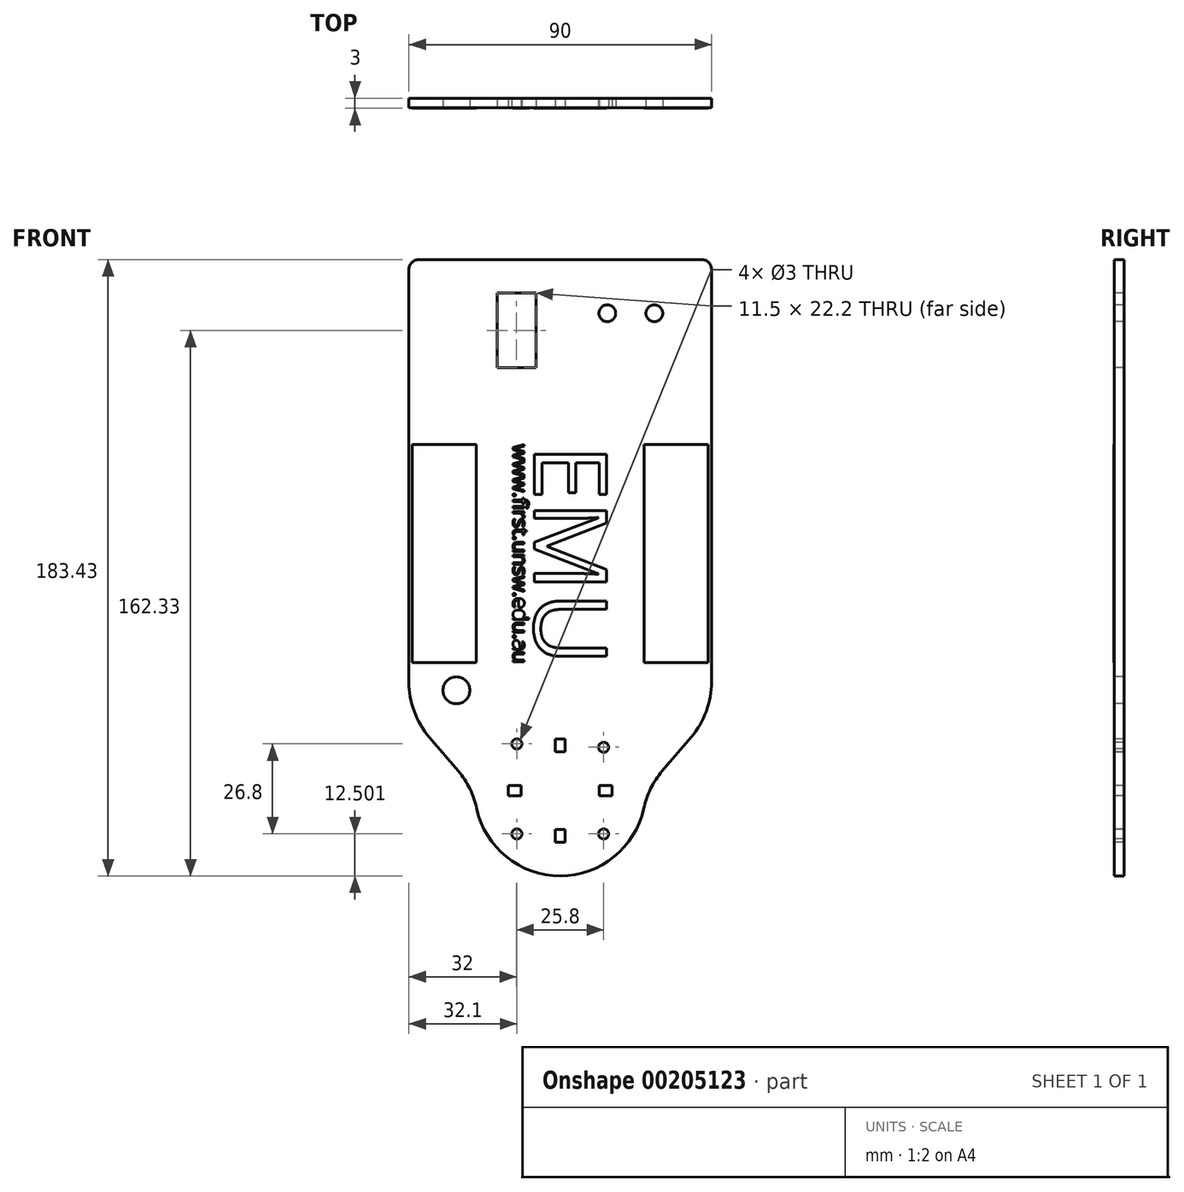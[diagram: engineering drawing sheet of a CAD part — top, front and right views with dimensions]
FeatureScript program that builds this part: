
annotation { "Feature Type Name" : "Feature", "Feature Type Description" : "" }
export const myFeature = defineFeature(function(context is Context, id is Id, definition is map)
    precondition{}
    {
        {
            var Q0;
            Q0=qCreatedBy(makeId("Front.planeOp"),FACE);
            var sketch = newSketch(context, id + "F0", { "sketchPlane" : qUnion([Q0])});
            skLineSegment(sketch, "E0.bottom", {"start": v(0, 0) * mm, "end": v(-90, 0) * mm});
            skLineSegment(sketch, "E0.top", {"start": v(0, 135) * mm, "end": v(-90, 135) * mm});
            skLineSegment(sketch, "E0.left", {"start": v(0, 0) * mm, "end": v(0, 135) * mm});
            skLineSegment(sketch, "E0.right", {"start": v(-90, 0) * mm, "end": v(-90, 135) * mm});
            skLineSegment(sketch, "E1", {"start": v(-90, 0) * mm, "end": v(-45, -70) * mm});
            skLineSegment(sketch, "E2", {"start": v(-45, -70) * mm, "end": v(0, 0) * mm});
            skSolve(sketch);
        }
        {
            var Q0;
            Q0=makeQuery(id+"F0.imprint","IMPRINT",FACE,{"disambiguationData":[TD([[makeQuery(id+"F0.imprint","IMPRINT",EDGE,{"derivedFrom":sQuery(id+"F0.wireOp",EDGE,"E0.bottom")}),-1.0]])]});
            var Q1;
            Q1=makeQuery(id+"F0.imprint","IMPRINT",FACE,{"disambiguationData":[TD([[makeQuery(id+"F0.imprint","IMPRINT",EDGE,{"derivedFrom":sQuery(id+"F0.wireOp",EDGE,"E0.bottom")}),1.0]])]});
            extrude(context, id + "F1", {"entities" : qUnion([Q0, Q1]), "depth" : 3 * mm});
        }
        {
            var Q0;
            Q0=makeQuery(id+"F1.opExtrude","CAP_FACE",FACE,{"disambiguationData":[OSD([sQuery(id+"F0.wireOp",EDGE,"E0.top"),sQuery(id+"F0.wireOp",EDGE,"E0.left"),sQuery(id+"F0.wireOp",EDGE,"E0.right"),sQuery(id+"F0.wireOp",EDGE,"E1"),sQuery(id+"F0.wireOp",EDGE,"E2")])],"isStart":false});
            var sketch = newSketch(context, id + "F2", { "sketchPlane" : qUnion([Q0])});
            skLineSegment(sketch, "E3.bottom", {"start": v(-63.75, 125) * mm, "end": v(-52.25, 125) * mm});
            skLineSegment(sketch, "E3.top", {"start": v(-63.75, 102.8) * mm, "end": v(-52.25, 102.8) * mm});
            skLineSegment(sketch, "E3.left", {"start": v(-63.75, 125) * mm, "end": v(-63.75, 102.8) * mm});
            skLineSegment(sketch, "E3.right", {"start": v(-52.25, 125) * mm, "end": v(-52.25, 102.8) * mm});
            skCircle(sketch, "E4", {"center": v(-58, 127) * mm, "radius": 1 * mm});
            skCircle(sketch, "E5", {"center": v(-58, 100.8) * mm, "radius": 1 * mm});
            skLineSegment(sketch, "E6", {"start": v(-59, 127) * mm, "end": v(-59, 125) * mm});
            skLineSegment(sketch, "E7", {"start": v(-57, 127) * mm, "end": v(-57, 125) * mm});
            skLineSegment(sketch, "E8", {"start": v(-59, 100.8) * mm, "end": v(-59, 102.8) * mm});
            skLineSegment(sketch, "E9", {"start": v(-57, 102.8) * mm, "end": v(-57, 100.8) * mm});
            skLineSegment(sketch, "E10", {"start": v(-45, 135) * mm, "end": v(-45, -52.75) * mm});
            skLineSegment(sketch, "E11", {"start": v(-58, 125) * mm, "end": v(-58, 102.8) * mm});
            skLineSegment(sketch, "E12", {"start": v(-63.75, 119) * mm, "end": v(-52.25, 119) * mm});
            skCircle(sketch, "E13", {"center": v(-31, 119) * mm, "radius": 2.5 * mm});
            skCircle(sketch, "E14", {"center": v(-17, 119) * mm, "radius": 2.5 * mm});
            skSolve(sketch);
        }
        {
            var Q0;
            {var subQ0=sQuery(id+"F2.wireOp",EDGE,"E3.left");Q0=makeQuery(id+"F2.imprint","IMPRINT",FACE,{"disambiguationData":[TD([[makeQuery(id+"F2.imprint","IMPRINT",EDGE,{"derivedFrom":subQ0}),1.0]])]});}
            var Q1;
            {var subQ1=sQuery(id+"F2.wireOp",EDGE,"E3.bottom");var subQ8=makeQuery(id+"F2.imprint","INTERSECT",VERTEX,{"derivedFrom":[subQ1,sQuery(id+"F2.wireOp",EDGE,"E7")]});Q1=makeQuery(id+"F2.imprint","IMPRINT",FACE,{"disambiguationData":[TD([[makeQuery(id+"F2.imprint","IMPRINT",EDGE,{"disambiguationData":[TD([[subQ8,1.0]])],"derivedFrom":subQ1}),-1.0]])]});}
            var Q2;
            {var subQ1=sQuery(id+"F2.wireOp",EDGE,"E3.top");var subQ7=makeQuery(id+"F2.imprint","INTERSECT",VERTEX,{"derivedFrom":[subQ1,sQuery(id+"F2.wireOp",EDGE,"E9")]});Q2=makeQuery(id+"F2.imprint","IMPRINT",FACE,{"disambiguationData":[TD([[makeQuery(id+"F2.imprint","IMPRINT",EDGE,{"disambiguationData":[TD([[subQ7,1.0]])],"derivedFrom":subQ1}),1.0]])]});}
            var Q3;
            Q3=makeQuery(id+"F2.imprint","IMPRINT",FACE,{"disambiguationData":[TD([[makeQuery(id+"F2.imprint","IMPRINT",EDGE,{"derivedFrom":sQuery(id+"F2.wireOp",EDGE,"E13")}),1.0]])]});
            var Q4;
            Q4=makeQuery(id+"F2.imprint","IMPRINT",FACE,{"disambiguationData":[TD([[makeQuery(id+"F2.imprint","IMPRINT",EDGE,{"derivedFrom":sQuery(id+"F2.wireOp",EDGE,"E14")}),1.0]])]});
            extrude(context, id + "F3", {"entities" : qUnion([Q0, Q1, Q2, Q3, Q4]), "operationType" : NewBodyOperationType.REMOVE, "oppositeDirection" : true, "depth" : 25.4 * mm});
        }
        {
            var Q0;
            Q0=makeQuery(id+"F1.opExtrude","SWEPT_EDGE",EDGE,{"disambiguationData":[OSD([sQuery(id+"F0.wireOp",EDGE,"E1"),sQuery(id+"F0.wireOp",EDGE,"E2")])]});
            fillet(context, id + "F4", {"entities" : qUnion([Q0]), "radius" : 25.4 * mm, "tangentPropagation" : true, "allowEdgeOverflow" : false});
        }
        {
            var Q0;
            Q0=makeQuery(id+"F1.opExtrude","CAP_FACE",FACE,{"disambiguationData":[OSD([sQuery(id+"F0.wireOp",EDGE,"E0.top"),sQuery(id+"F0.wireOp",EDGE,"E0.left"),sQuery(id+"F0.wireOp",EDGE,"E0.right"),sQuery(id+"F0.wireOp",EDGE,"E1"),sQuery(id+"F0.wireOp",EDGE,"E2")])],"isStart":false});
            var sketch = newSketch(context, id + "F5", { "sketchPlane" : qUnion([Q0])});
            skCircle(sketch, "E15", {"center": v(-45, -23.03) * mm, "radius": 25.4 * mm});
            skLineSegment(sketch, "E16", {"start": v(-45, -48.43) * mm, "end": v(-45, 2.37) * mm});
            skLineSegment(sketch, "E17", {"start": v(-45, -23.03) * mm, "end": v(-19.6, -23.03) * mm});
            skLineSegment(sketch, "E18", {"start": v(-45, -23.03) * mm, "end": v(-70.4, -23.03) * mm});
            skLineSegment(sketch, "E19.bottom", {"start": v(-60.4, -24.53) * mm, "end": v(-56.59, -24.53) * mm});
            skLineSegment(sketch, "E19.top", {"start": v(-60.4, -21.53) * mm, "end": v(-56.59, -21.53) * mm});
            skLineSegment(sketch, "E19.left", {"start": v(-60.4, -24.53) * mm, "end": v(-60.4, -21.53) * mm});
            skLineSegment(sketch, "E19.right", {"start": v(-56.59, -24.53) * mm, "end": v(-56.59, -21.53) * mm});
            skLineSegment(sketch, "E20.bottom", {"start": v(-46.5, -11.44) * mm, "end": v(-43.5, -11.44) * mm});
            skLineSegment(sketch, "E20.top", {"start": v(-46.5, -7.63) * mm, "end": v(-43.5, -7.63) * mm});
            skLineSegment(sketch, "E20.left", {"start": v(-46.5, -11.44) * mm, "end": v(-46.5, -7.63) * mm});
            skLineSegment(sketch, "E20.right", {"start": v(-43.5, -11.44) * mm, "end": v(-43.5, -7.63) * mm});
            skLineSegment(sketch, "E21.bottom", {"start": v(-33.4, -21.53) * mm, "end": v(-29.6, -21.53) * mm});
            skLineSegment(sketch, "E21.top", {"start": v(-33.4, -24.53) * mm, "end": v(-29.6, -24.53) * mm});
            skLineSegment(sketch, "E21.left", {"start": v(-33.4, -21.53) * mm, "end": v(-33.4, -24.53) * mm});
            skLineSegment(sketch, "E21.right", {"start": v(-29.6, -21.53) * mm, "end": v(-29.6, -24.53) * mm});
            skLineSegment(sketch, "E22.bottom", {"start": v(-46.5, -34.62) * mm, "end": v(-43.5, -34.62) * mm});
            skLineSegment(sketch, "E22.top", {"start": v(-46.5, -38.43) * mm, "end": v(-43.5, -38.43) * mm});
            skLineSegment(sketch, "E22.left", {"start": v(-46.5, -34.62) * mm, "end": v(-46.5, -38.43) * mm});
            skLineSegment(sketch, "E22.right", {"start": v(-43.5, -34.62) * mm, "end": v(-43.5, -38.43) * mm});
            skLineSegment(sketch, "E23", {"start": v(-45, -3.98) * mm, "end": v(-45, -11.44) * mm});
            skCircle(sketch, "E24", {"center": v(-57.9, -9.13) * mm, "radius": 1.5 * mm});
            skCircle(sketch, "E25", {"center": v(-32.1, -10.13) * mm, "radius": 1.5 * mm});
            skCircle(sketch, "E26", {"center": v(-32.1, -35.93) * mm, "radius": 1.5 * mm});
            skCircle(sketch, "E27", {"center": v(-57.9, -35.93) * mm, "radius": 1.5 * mm});
            skSolve(sketch);
        }
        {
            var Q0;
            {var subQ5=sQuery(id+"F5.wireOp",EDGE,"E19.top");Q0=makeQuery(id+"F5.imprint","IMPRINT",FACE,{"disambiguationData":[TD([[makeQuery(id+"F5.imprint","IMPRINT",EDGE,{"derivedFrom":subQ5}),-1.0]])]});}
            var Q1;
            {var subQ5=sQuery(id+"F5.wireOp",EDGE,"E19.bottom");Q1=makeQuery(id+"F5.imprint","IMPRINT",FACE,{"disambiguationData":[TD([[makeQuery(id+"F5.imprint","IMPRINT",EDGE,{"derivedFrom":subQ5}),1.0]])]});}
            var Q2;
            {var subQ5=sQuery(id+"F5.wireOp",EDGE,"E21.bottom");Q2=makeQuery(id+"F5.imprint","IMPRINT",FACE,{"disambiguationData":[TD([[makeQuery(id+"F5.imprint","IMPRINT",EDGE,{"derivedFrom":subQ5}),-1.0]])]});}
            var Q3;
            {var subQ5=sQuery(id+"F5.wireOp",EDGE,"E21.top");Q3=makeQuery(id+"F5.imprint","IMPRINT",FACE,{"disambiguationData":[TD([[makeQuery(id+"F5.imprint","IMPRINT",EDGE,{"derivedFrom":subQ5}),1.0]])]});}
            var Q4;
            {var subQ5=sQuery(id+"F5.wireOp",EDGE,"E22.right");Q4=makeQuery(id+"F5.imprint","IMPRINT",FACE,{"disambiguationData":[TD([[makeQuery(id+"F5.imprint","IMPRINT",EDGE,{"derivedFrom":subQ5}),-1.0]])]});}
            var Q5;
            {var subQ5=sQuery(id+"F5.wireOp",EDGE,"E22.left");Q5=makeQuery(id+"F5.imprint","IMPRINT",FACE,{"disambiguationData":[TD([[makeQuery(id+"F5.imprint","IMPRINT",EDGE,{"derivedFrom":subQ5}),1.0]])]});}
            var Q6;
            {var subQ5=sQuery(id+"F5.wireOp",EDGE,"E20.right");Q6=makeQuery(id+"F5.imprint","IMPRINT",FACE,{"disambiguationData":[TD([[makeQuery(id+"F5.imprint","IMPRINT",EDGE,{"derivedFrom":subQ5}),1.0]])]});}
            var Q7;
            {var subQ5=sQuery(id+"F5.wireOp",EDGE,"E20.left");Q7=makeQuery(id+"F5.imprint","IMPRINT",FACE,{"disambiguationData":[TD([[makeQuery(id+"F5.imprint","IMPRINT",EDGE,{"derivedFrom":subQ5}),-1.0]])]});}
            var Q8;
            {var subQ5=sQuery(id+"F5.wireOp",EDGE,"Zrzo9GHM-fuN2-8fML-iVZU-LCXHQRcVOfyt.left");Q8=makeQuery(id+"F5.imprint","IMPRINT",FACE,{"disambiguationData":[TD([[makeQuery(id+"F5.imprint","IMPRINT",EDGE,{"derivedFrom":subQ5}),1.0]])]});}
            var Q9;
            {var subQ5=sQuery(id+"F5.wireOp",EDGE,"Zrzo9GHM-fuN2-8fML-iVZU-LCXHQRcVOfyt.right");Q9=makeQuery(id+"F5.imprint","IMPRINT",FACE,{"disambiguationData":[TD([[makeQuery(id+"F5.imprint","IMPRINT",EDGE,{"derivedFrom":subQ5}),-1.0]])]});}
            var Q10;
            {var subQ0=sQuery(id+"F5.wireOp",EDGE,"2EuhVOSW-e1DR-vE8P-bMp6-yslpzd3IsdpB");var subQ4=makeQuery(id+"F5.imprint","IMPRINT",VERTEX,{"derivedFrom":subQ0});Q10=makeQuery(id+"F5.imprint","IMPRINT",FACE,{"disambiguationData":[TD([[makeQuery(id+"F5.imprint","IMPRINT",EDGE,{"disambiguationData":[TD([[subQ4,1.0]])],"derivedFrom":subQ0}),-1.0]])]});}
            var Q11;
            {var subQ0=sQuery(id+"F5.wireOp",EDGE,"2EuhVOSW-e1DR-vE8P-bMp6-yslpzd3IsdpB");var subQ4=makeQuery(id+"F5.imprint","IMPRINT",VERTEX,{"derivedFrom":subQ0});Q11=makeQuery(id+"F5.imprint","IMPRINT",FACE,{"disambiguationData":[TD([[makeQuery(id+"F5.imprint","IMPRINT",EDGE,{"disambiguationData":[TD([[subQ4,1.0]])],"derivedFrom":subQ0}),1.0]])]});}
            var Q12;
            Q12=makeQuery(id+"F5.imprint","IMPRINT",FACE,{"disambiguationData":[TD([[makeQuery(id+"F5.imprint","IMPRINT",EDGE,{"derivedFrom":sQuery(id+"F5.wireOp",EDGE,"E24")}),1.0]])]});
            var Q13;
            Q13=makeQuery(id+"F5.imprint","IMPRINT",FACE,{"disambiguationData":[TD([[makeQuery(id+"F5.imprint","IMPRINT",EDGE,{"derivedFrom":sQuery(id+"F5.wireOp",EDGE,"E25")}),1.0]])]});
            var Q14;
            Q14=makeQuery(id+"F5.imprint","IMPRINT",FACE,{"disambiguationData":[TD([[makeQuery(id+"F5.imprint","IMPRINT",EDGE,{"derivedFrom":sQuery(id+"F5.wireOp",EDGE,"E26")}),1.0]])]});
            var Q15;
            Q15=makeQuery(id+"F5.imprint","IMPRINT",FACE,{"disambiguationData":[TD([[makeQuery(id+"F5.imprint","IMPRINT",EDGE,{"derivedFrom":sQuery(id+"F5.wireOp",EDGE,"E27")}),1.0]])]});
            extrude(context, id + "F6", {"entities" : qUnion([Q0, Q1, Q2, Q3, Q4, Q5, Q6, Q7, Q8, Q9, Q10, Q11, Q12, Q13, Q14, Q15]), "operationType" : NewBodyOperationType.REMOVE, "oppositeDirection" : true, "depth" : 25.4 * mm});
        }
        {
            var Q0;
            Q0=makeQuery(id+"F1.opExtrude","SWEPT_EDGE",EDGE,{"disambiguationData":[OSD([sQuery(id+"F0.wireOp",EDGE,"E0.top"),sQuery(id+"F0.wireOp",EDGE,"E0.left")])]});
            var Q1;
            Q1=makeQuery(id+"F1.opExtrude","SWEPT_EDGE",EDGE,{"disambiguationData":[OSD([sQuery(id+"F0.wireOp",EDGE,"E0.top"),sQuery(id+"F0.wireOp",EDGE,"E0.right")])]});
            fillet(context, id + "F7", {"entities" : qUnion([Q0, Q1]), "radius" : 3 * mm, "tangentPropagation" : true, "allowEdgeOverflow" : false});
        }
        {
            var Q0;
            Q0=makeQuery(id+"F1.opExtrude","CAP_FACE",FACE,{"disambiguationData":[OSD([sQuery(id+"F0.wireOp",EDGE,"E0.top"),sQuery(id+"F0.wireOp",EDGE,"E0.left"),sQuery(id+"F0.wireOp",EDGE,"E0.right"),sQuery(id+"F0.wireOp",EDGE,"E1"),sQuery(id+"F0.wireOp",EDGE,"E2")])],"isStart":false});
            var sketch = newSketch(context, id + "F8", { "sketchPlane" : qUnion([Q0])});
            skCircle(sketch, "E28", {"center": v(-45, -23.03) * mm, "radius": 25.4 * mm});
            skLineSegment(sketch, "E29", {"start": v(-45, -23.03) * mm, "end": v(-70.4, -23.03) * mm});
            skLineSegment(sketch, "E30", {"start": v(-45, -23.03) * mm, "end": v(-19.6, -23.03) * mm});
            skLineSegment(sketch, "E31", {"start": v(-70.4, -23.03) * mm, "end": v(-90, 0) * mm});
            skLineSegment(sketch, "E32", {"start": v(-19.6, -23.03) * mm, "end": v(0, 0) * mm});
            skSolve(sketch);
        }
        {
            var Q0;
            {var subQ2=sQuery(id+"F8.wireOp",EDGE,"E31");Q0=makeQuery(id+"F8.imprint","IMPRINT",FACE,{"disambiguationData":[TD([[makeQuery(id+"F8.imprint","IMPRINT",EDGE,{"derivedFrom":subQ2}),1.0]])]});}
            var Q1;
            {var subQ2=sQuery(id+"F8.wireOp",EDGE,"E32");Q1=makeQuery(id+"F8.imprint","IMPRINT",FACE,{"disambiguationData":[TD([[makeQuery(id+"F8.imprint","IMPRINT",EDGE,{"derivedFrom":subQ2}),-1.0]])]});}
            extrude(context, id + "F9", {"entities" : qUnion([Q0, Q1]), "operationType" : NewBodyOperationType.REMOVE, "oppositeDirection" : true, "depth" : 25.4 * mm});
        }
        {
            var Q0;
            Q0=makeQuery(id+"F9.boolean.opBoolean","COPY",EDGE,{"derivedFrom":makeQuery(id+"F9.opExtrude","SWEPT_EDGE",EDGE,{"disambiguationData":[OSD([sQuery(id+"F8.wireOp",EDGE,"E28"),sQuery(id+"F8.wireOp",EDGE,"E29"),sQuery(id+"F8.wireOp",EDGE,"E31")])]})});
            var Q1;
            {var subQ0=sQuery(id+"F0.wireOp",EDGE,"E1");var subQ1=sQuery(id+"F0.wireOp",EDGE,"E0.right");Q1=makeQuery(id+"F9.boolean.opBoolean","MERGE",EDGE,{"derivedFrom":[makeQuery(id+"F1.opExtrude","SWEPT_EDGE",EDGE,{"disambiguationData":[OSD([sQuery(id+"F0.wireOp",EDGE,"E0.bottom"),subQ1,subQ0])]}),makeQuery(id+"F9.opExtrude","SWEPT_EDGE",EDGE,{"disambiguationData":[OSD([subQ1,subQ0,sQuery(id+"F8.wireOp",EDGE,"E31")])]})]});}
            var Q2;
            Q2=makeQuery(id+"F9.boolean.opBoolean","COPY",EDGE,{"derivedFrom":makeQuery(id+"F9.opExtrude","SWEPT_EDGE",EDGE,{"disambiguationData":[OSD([sQuery(id+"F8.wireOp",EDGE,"E28"),sQuery(id+"F8.wireOp",EDGE,"E30"),sQuery(id+"F8.wireOp",EDGE,"E32")])]})});
            var Q3;
            {var subQ0=sQuery(id+"F0.wireOp",EDGE,"E2");var subQ1=sQuery(id+"F0.wireOp",EDGE,"E0.left");Q3=makeQuery(id+"F9.boolean.opBoolean","MERGE",EDGE,{"derivedFrom":[makeQuery(id+"F1.opExtrude","SWEPT_EDGE",EDGE,{"disambiguationData":[OSD([sQuery(id+"F0.wireOp",EDGE,"E0.bottom"),subQ1,subQ0])]}),makeQuery(id+"F9.opExtrude","SWEPT_EDGE",EDGE,{"disambiguationData":[OSD([subQ1,subQ0,sQuery(id+"F8.wireOp",EDGE,"E32")])]})]});}
            fillet(context, id + "F10", {"entities" : qUnion([Q0, Q1, Q2, Q3]), "radius" : 25.4 * mm, "tangentPropagation" : true, "allowEdgeOverflow" : false});
        }
        {
            var Q0;
            Q0=makeQuery(id+"F1.opExtrude","CAP_FACE",FACE,{"disambiguationData":[OSD([sQuery(id+"F0.wireOp",EDGE,"E0.top"),sQuery(id+"F0.wireOp",EDGE,"E0.left"),sQuery(id+"F0.wireOp",EDGE,"E0.right"),sQuery(id+"F0.wireOp",EDGE,"E1"),sQuery(id+"F0.wireOp",EDGE,"E2")])],"isStart":false});
            var sketch = newSketch(context, id + "F11", { "sketchPlane" : qUnion([Q0])});
            skLineSegment(sketch, "E33", {"start": v(-89.87, 6.8) * mm, "end": v(-75.87, 6.8) * mm});
            skCircle(sketch, "E34", {"center": v(-75.87, 6.8) * mm, "radius": 4 * mm});
            skSolve(sketch);
        }
        {
            var Q0;
            Q0=makeQuery(id+"F11.imprint","IMPRINT",FACE,{"disambiguationData":[TD([[makeQuery(id+"F11.imprint","IMPRINT",EDGE,{"derivedFrom":sQuery(id+"F11.wireOp",EDGE,"E34")}),1.0]])]});
            extrude(context, id + "F12", {"entities" : qUnion([Q0]), "operationType" : NewBodyOperationType.REMOVE, "oppositeDirection" : true, "depth" : 3 * mm});
        }
        {
            var Q0;
            Q0=makeQuery(id+"F1.opExtrude","CAP_FACE",FACE,{"disambiguationData":[OSD([sQuery(id+"F0.wireOp",EDGE,"E0.top"),sQuery(id+"F0.wireOp",EDGE,"E0.left"),sQuery(id+"F0.wireOp",EDGE,"E0.right"),sQuery(id+"F0.wireOp",EDGE,"E1"),sQuery(id+"F0.wireOp",EDGE,"E2")])],"isStart":false});
            var sketch = newSketch(context, id + "F13", { "sketchPlane" : qUnion([Q0])});
            skLineSegment(sketch, "E35.bottom", {"start": v(-90, 80) * mm, "end": v(-70, 80) * mm});
            skLineSegment(sketch, "E35.top", {"start": v(-90, 15) * mm, "end": v(-70, 15) * mm});
            skLineSegment(sketch, "E35.left", {"start": v(-90, 80) * mm, "end": v(-90, 15) * mm});
            skLineSegment(sketch, "E35.right", {"start": v(-70, 80) * mm, "end": v(-70, 15) * mm});
            skLineSegment(sketch, "E36.bottom", {"start": v(0, 15) * mm, "end": v(-20, 15) * mm});
            skLineSegment(sketch, "E36.top", {"start": v(0, 80) * mm, "end": v(-20, 80) * mm});
            skLineSegment(sketch, "E36.left", {"start": v(0, 15) * mm, "end": v(0, 80) * mm});
            skLineSegment(sketch, "E36.right", {"start": v(-20, 15) * mm, "end": v(-20, 80) * mm});
            skLineSegment(sketch, "E37", {"start": v(-1, 15) * mm, "end": v(-1, 80) * mm});
            skLineSegment(sketch, "E38", {"start": v(-89, 15) * mm, "end": v(-89, 80) * mm});
            skText(sketch, "E39", { "text": "EMU", "fontName": "OpenSans-Regular.ttf"});
            skPoint(sketch, "E39.firstSnap0", {"position": v(-58, 102.8) * mm});
            skPoint(sketch, "E39.secondSnap0", {"position": v(-10, 15) * mm});
            skLineSegment(sketch, "E40", {"start": v(-41.83, 47.5) * mm, "end": v(-41.83, 49.9) * mm});
            skPoint(sketch, "E41", {"position": v(-70, 47.5) * mm});
            skText(sketch, "E42", { "text": "www.first.unsw.edu.au", "fontName": "OpenSans-Regular.ttf"});
            skLineSegment(sketch, "E43", {"start": v(-56.8, 47.5) * mm, "end": v(-56.8, 48.11) * mm});
            const initialGuessF13  = {"E39": [-0.05266, 0.08, 0, -1, 0.02166], "E42": [-0.059, 0.08, 0, -1, 0.0044]};
            skSetInitialGuess(sketch, initialGuessF13);
            skSolve(sketch);
        }
        {
            var Q0;
            {var subQ11=sQuery(id+"F13.wireOp",EDGE,"E35.right");Q0=makeQuery(id+"F13.imprint","IMPRINT",FACE,{"disambiguationData":[TD([[makeQuery(id+"F13.imprint","IMPRINT",EDGE,{"derivedFrom":subQ11}),1.0]])]});}
            var Q1;
            {var subQ0=sQuery(id+"F13.wireOp",EDGE,"E35.left");Q1=makeQuery(id+"F13.imprint","IMPRINT",FACE,{"disambiguationData":[TD([[makeQuery(id+"F13.imprint","IMPRINT",EDGE,{"derivedFrom":subQ0}),-1.0]])]});}
            var Q2;
            {var subQ0=sQuery(id+"F13.wireOp",EDGE,"E36.left");Q2=makeQuery(id+"F13.imprint","IMPRINT",FACE,{"disambiguationData":[TD([[makeQuery(id+"F13.imprint","IMPRINT",EDGE,{"derivedFrom":subQ0}),1.0]])]});}
            extrude(context, id + "F14", {"entities" : qUnion([Q0, Q1, Q2]), "operationType" : NewBodyOperationType.REMOVE, "oppositeDirection" : true, "depth" : .1 * mm});
        }
    });
